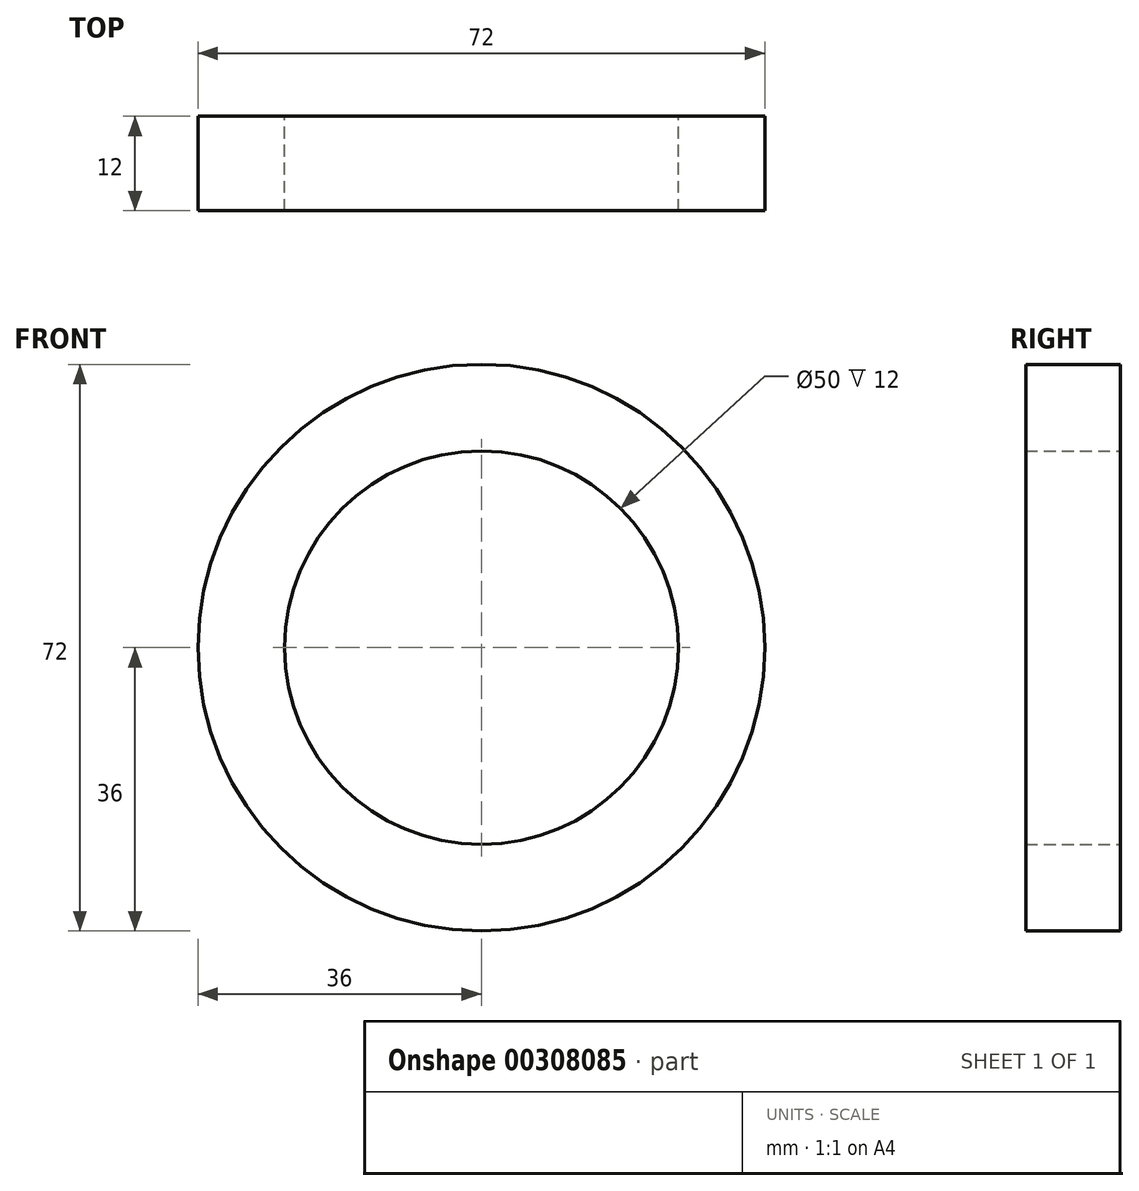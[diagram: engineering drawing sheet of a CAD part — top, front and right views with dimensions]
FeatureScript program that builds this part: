
annotation { "Feature Type Name" : "Feature", "Feature Type Description" : "" }
export const myFeature = defineFeature(function(context is Context, id is Id, definition is map)
    precondition{}
    {
        {
            var Q0;
            Q0=qCreatedBy(makeId("Front.planeOp"),FACE);
            var sketch = newSketch(context, id + "F0", { "sketchPlane" : qUnion([Q0])});
            skCircle(sketch, "E0", {"center": v(0, 0) * mm, "radius": 36 * mm});
            skCircle(sketch, "E1", {"center": v(0, 0) * mm, "radius": 25 * mm});
            skSolve(sketch);
        }
        {
            var Q0;
            Q0 = qSketchRegion(id + "F0", true);
            extrude(context, id + "F1", {"entities" : qUnion([Q0]), "depth" : 12 * mm, "offsetDistance" : 25.4 * mm});
        }
    });
